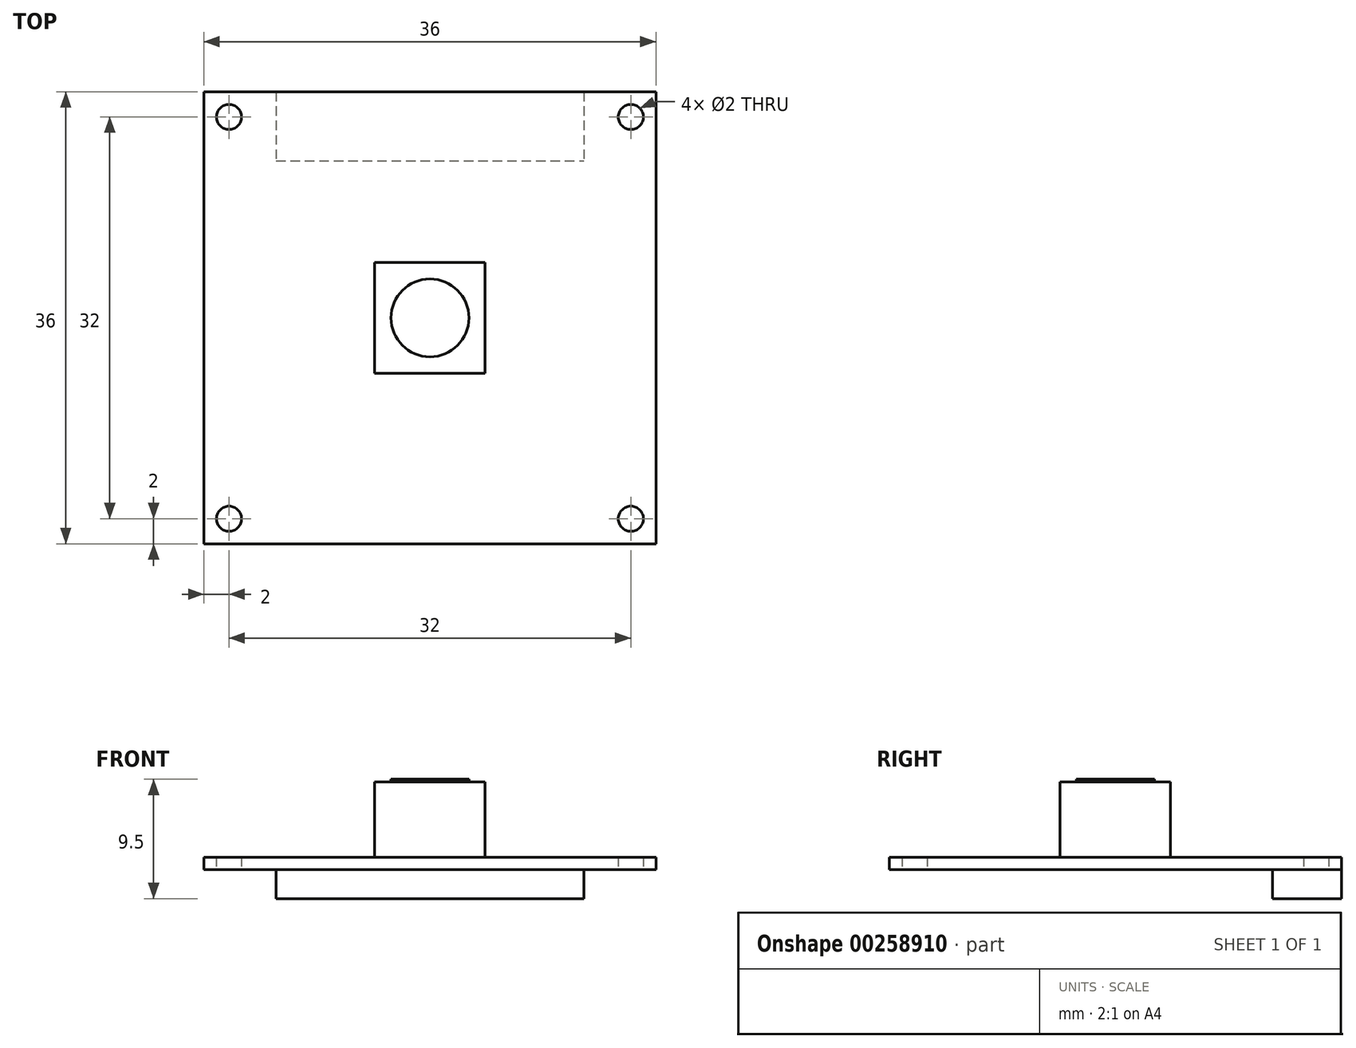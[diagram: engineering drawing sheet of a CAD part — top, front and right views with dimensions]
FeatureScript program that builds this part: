
annotation { "Feature Type Name" : "Feature", "Feature Type Description" : "" }
export const myFeature = defineFeature(function(context is Context, id is Id, definition is map)
    precondition{}
    {
        {
            var Q0;
            Q0=qCreatedBy(makeId("Top.planeOp"),FACE);
            var sketch = newSketch(context, id + "F0", { "sketchPlane" : qUnion([Q0])});
            skLineSegment(sketch, "E0.bottom", {"start": v(-18, -18) * mm, "end": v(18, -18) * mm});
            skLineSegment(sketch, "E0.top", {"start": v(-18, 18) * mm, "end": v(18, 18) * mm});
            skLineSegment(sketch, "E0.left", {"start": v(-18, -18) * mm, "end": v(-18, 18) * mm});
            skLineSegment(sketch, "E0.right", {"start": v(18, -18) * mm, "end": v(18, 18) * mm});
            skPoint(sketch, "E0.middle", {"position": v(0, 0) * mm});
            skCircle(sketch, "E1", {"center": v(-16, 16) * mm, "radius": 1 * mm});
            skCircle(sketch, "E2.MirrorC", {"center": v(16, 16) * mm, "radius": 1 * mm});
            skCircle(sketch, "E3.MirrorC", {"center": v(-16, -16) * mm, "radius": 1 * mm});
            skCircle(sketch, "E4.MirrorC", {"center": v(16, -16) * mm, "radius": 1 * mm});
            skSolve(sketch);
        }
        {
            var Q0;
            Q0 = qSketchRegion(id + "F0", true);
            extrude(context, id + "F1", {"entities" : qUnion([Q0]), "depth" : 1 * mm});
        }
        {
            var Q0;
            Q0=makeQuery(id+"F1.opExtrude","CAP_FACE",FACE,{"disambiguationData":[OSD([sQuery(id+"F0.wireOp",EDGE,"E0.bottom"),sQuery(id+"F0.wireOp",EDGE,"E0.top"),sQuery(id+"F0.wireOp",EDGE,"E0.left"),sQuery(id+"F0.wireOp",EDGE,"E0.right"),sQuery(id+"F0.wireOp",EDGE,"E1"),sQuery(id+"F0.wireOp",EDGE,"E2.MirrorC"),sQuery(id+"F0.wireOp",EDGE,"E3.MirrorC"),sQuery(id+"F0.wireOp",EDGE,"E4.MirrorC")])],"isStart":false});
            var sketch = newSketch(context, id + "F2", { "sketchPlane" : qUnion([Q0])});
            skLineSegment(sketch, "E5.bottom", {"start": v(-4.4, -4.4) * mm, "end": v(4.4, -4.4) * mm});
            skLineSegment(sketch, "E5.top", {"start": v(-4.4, 4.4) * mm, "end": v(4.4, 4.4) * mm});
            skLineSegment(sketch, "E5.left", {"start": v(-4.4, -4.4) * mm, "end": v(-4.4, 4.4) * mm});
            skLineSegment(sketch, "E5.right", {"start": v(4.4, -4.4) * mm, "end": v(4.4, 4.4) * mm});
            skPoint(sketch, "E5.middle", {"position": v(0, 0) * mm});
            skSolve(sketch);
        }
        {
            var Q0;
            Q0 = qSketchRegion(id + "F2", true);
            extrude(context, id + "F3", {"entities" : qUnion([Q0]), "operationType" : NewBodyOperationType.ADD, "depth" : 6 * mm});
        }
        {
            var Q0;
            Q0=makeQuery(id+"F1.opExtrude","CAP_FACE",FACE,{"disambiguationData":[OSD([sQuery(id+"F0.wireOp",EDGE,"E0.bottom"),sQuery(id+"F0.wireOp",EDGE,"E0.top"),sQuery(id+"F0.wireOp",EDGE,"E0.left"),sQuery(id+"F0.wireOp",EDGE,"E0.right"),sQuery(id+"F0.wireOp",EDGE,"E1"),sQuery(id+"F0.wireOp",EDGE,"E2.MirrorC"),sQuery(id+"F0.wireOp",EDGE,"E3.MirrorC"),sQuery(id+"F0.wireOp",EDGE,"E4.MirrorC")])],"isStart":true});
            var sketch = newSketch(context, id + "F4", { "sketchPlane" : qUnion([Q0])});
            skLineSegment(sketch, "E6.bottom", {"start": v(-12.25, -18) * mm, "end": v(12.25, -18) * mm});
            skLineSegment(sketch, "E6.top", {"start": v(-12.25, -12.5) * mm, "end": v(12.25, -12.5) * mm});
            skLineSegment(sketch, "E6.left", {"start": v(-12.25, -18) * mm, "end": v(-12.25, -12.5) * mm});
            skLineSegment(sketch, "E6.right", {"start": v(12.25, -18) * mm, "end": v(12.25, -12.5) * mm});
            skPoint(sketch, "E7", {"position": v(0, -12.5) * mm});
            skSolve(sketch);
        }
        {
            var Q0;
            Q0 = qSketchRegion(id + "F4", true);
            extrude(context, id + "F5", {"entities" : qUnion([Q0]), "operationType" : NewBodyOperationType.ADD, "depth" : 2.3 * mm});
        }
        {
            var Q0;
            Q0=makeQuery(id+"F3.opExtrude","CAP_FACE",FACE,{"disambiguationData":[OSD([sQuery(id+"F2.wireOp",EDGE,"E5.bottom"),sQuery(id+"F2.wireOp",EDGE,"E5.top"),sQuery(id+"F2.wireOp",EDGE,"E5.left"),sQuery(id+"F2.wireOp",EDGE,"E5.right")])],"isStart":false});
            var sketch = newSketch(context, id + "F6", { "sketchPlane" : qUnion([Q0])});
            skCircle(sketch, "E8", {"center": v(0, 0) * mm, "radius": 3.1 * mm});
            skSolve(sketch);
        }
        {
            var Q0;
            Q0 = qSketchRegion(id + "F6", true);
            extrude(context, id + "F7", {"entities" : qUnion([Q0]), "operationType" : NewBodyOperationType.ADD, "depth" : 0.2 * mm});
        }
    });
